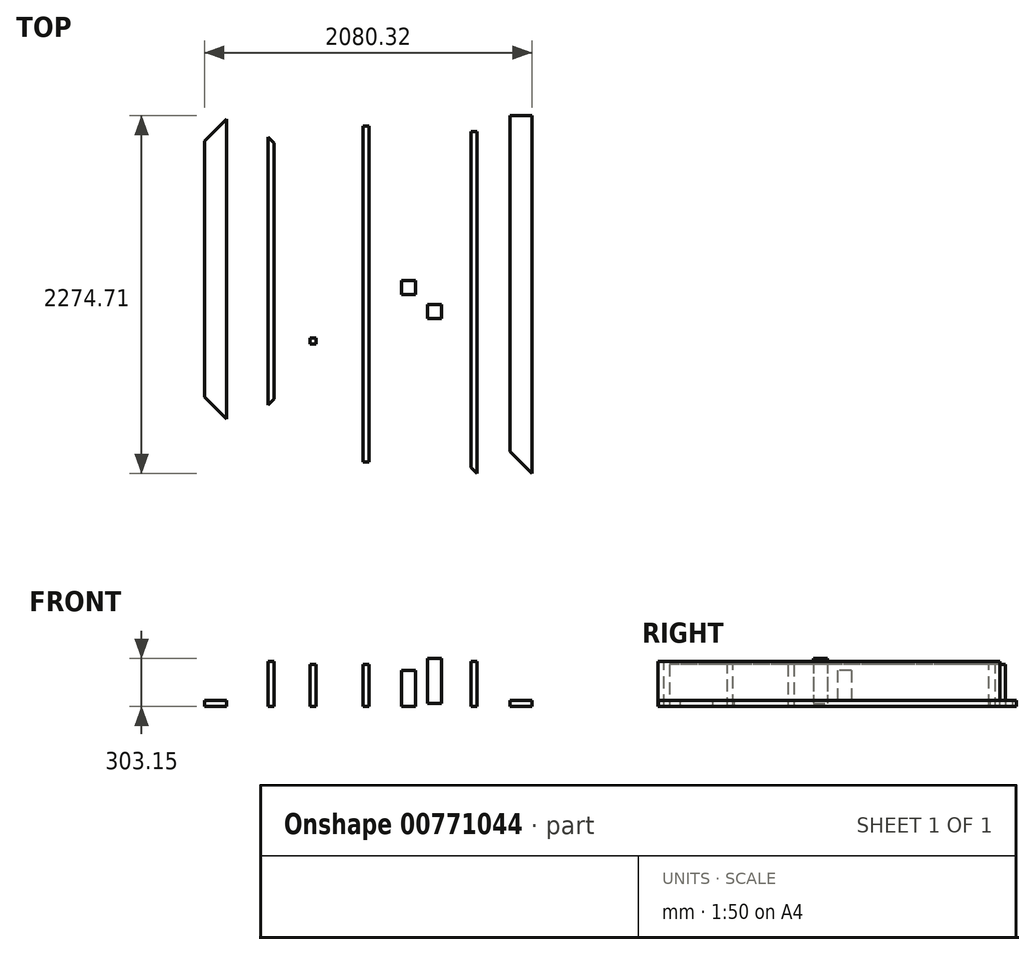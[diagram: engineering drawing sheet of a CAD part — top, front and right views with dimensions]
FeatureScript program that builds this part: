
annotation { "Feature Type Name" : "Feature", "Feature Type Description" : "" }
export const myFeature = defineFeature(function(context is Context, id is Id, definition is map)
    precondition{}
    {
        {
            var Q0;
            Q0=qCreatedBy(makeId("Top.planeOp"),FACE);
            var sketch = newSketch(context, id + "F0", { "sketchPlane" : qUnion([Q0])});
            skLineSegment(sketch, "E0.bottom", {"start": v(19.05, -1075.68) * mm, "end": v(-19.05, -1075.68) * mm});
            skLineSegment(sketch, "E0.top", {"start": v(19.05, 1134.12) * mm, "end": v(-19.05, 1134.12) * mm});
            skLineSegment(sketch, "E0.left", {"start": v(19.05, -1075.68) * mm, "end": v(19.05, 1134.12) * mm});
            skLineSegment(sketch, "E0.right", {"start": v(-19.05, -1075.68) * mm, "end": v(-19.05, 1134.12) * mm});
            skPoint(sketch, "E0.middle", {"position": v(0, 29.22) * mm});
            skSolve(sketch);
        }
        {
            var Q0;
            Q0=makeQuery(id+"F0.imprint","IMPRINT",FACE,{"disambiguationData":[TD([[makeQuery(id+"F0.imprint","IMPRINT",EDGE,{"derivedFrom":sQuery(id+"F0.wireOp",EDGE,"E0.bottom")}),-1.0]])]});
            extrude(context, id + "F1", {"entities" : qUnion([Q0]), "depth" : 285.75 * mm, "offsetDistance" : 25.4 * mm});
        }
        {
            var Q0;
            Q0=makeQuery(id+"F1.opExtrude","CAP_FACE",FACE,{"disambiguationData":[OSD([sQuery(id+"F0.wireOp",EDGE,"E0.bottom"),sQuery(id+"F0.wireOp",EDGE,"E0.top"),sQuery(id+"F0.wireOp",EDGE,"E0.left"),sQuery(id+"F0.wireOp",EDGE,"E0.right")])],"isStart":false});
            var sketch = newSketch(context, id + "F2", { "sketchPlane" : qUnion([Q0])});
            skLineSegment(sketch, "E1", {"start": v(19.05, -1075.68) * mm, "end": v(-19.05, -1075.68) * mm});
            skLineSegment(sketch, "E2", {"start": v(-19.05, -1075.68) * mm, "end": v(-19.05, -1037.58) * mm});
            skLineSegment(sketch, "E3", {"start": v(-19.05, -1037.58) * mm, "end": v(19.05, -1075.68) * mm});
            skSolve(sketch);
        }
        {
            var Q0;
            Q0=makeQuery(id+"F2.imprint","IMPRINT",FACE,{"disambiguationData":[TD([[makeQuery(id+"F2.imprint","IMPRINT",EDGE,{"derivedFrom":sQuery(id+"F2.wireOp",EDGE,"E1")}),-1.0]])]});
            extrude(context, id + "F3", {"entities" : qUnion([Q0]), "operationType" : NewBodyOperationType.REMOVE, "endBound" : BoundingType.THROUGH_ALL, "oppositeDirection" : true, "depth" : 25.4 * mm, "offsetDistance" : 25.4 * mm});
        }
        {
            var Q0;
            Q0=qCreatedBy(makeId("Top.planeOp"),FACE);
            var sketch = newSketch(context, id + "F4", { "sketchPlane" : qUnion([Q0])});
            skLineSegment(sketch, "E4.bottom", {"start": v(-1308.24, 1062.83) * mm, "end": v(-1270.14, 1062.83) * mm});
            skLineSegment(sketch, "E4.top", {"start": v(-1308.24, -638.97) * mm, "end": v(-1270.14, -638.97) * mm});
            skLineSegment(sketch, "E4.left", {"start": v(-1308.24, 1062.83) * mm, "end": v(-1308.24, -638.97) * mm});
            skLineSegment(sketch, "E4.right", {"start": v(-1270.14, 1062.83) * mm, "end": v(-1270.14, -638.97) * mm});
            skSolve(sketch);
        }
        {
            var Q0;
            Q0=makeQuery(id+"F4.imprint","IMPRINT",FACE,{"disambiguationData":[TD([[makeQuery(id+"F4.imprint","IMPRINT",EDGE,{"derivedFrom":sQuery(id+"F4.wireOp",EDGE,"E4.bottom")}),-1.0]])]});
            extrude(context, id + "F5", {"entities" : qUnion([Q0]), "depth" : 285.75 * mm, "offsetDistance" : 25.4 * mm});
        }
        {
            var Q0;
            Q0=makeQuery(id+"F5.opExtrude","CAP_FACE",FACE,{"disambiguationData":[OSD([sQuery(id+"F4.wireOp",EDGE,"E4.bottom"),sQuery(id+"F4.wireOp",EDGE,"E4.top"),sQuery(id+"F4.wireOp",EDGE,"E4.left"),sQuery(id+"F4.wireOp",EDGE,"E4.right")])],"isStart":false});
            var sketch = newSketch(context, id + "F6", { "sketchPlane" : qUnion([Q0])});
            skLineSegment(sketch, "E5", {"start": v(-1270.14, 1062.83) * mm, "end": v(-1308.24, 1062.83) * mm});
            skLineSegment(sketch, "E6", {"start": v(-1308.24, 1062.83) * mm, "end": v(-1270.14, 1024.73) * mm});
            skLineSegment(sketch, "E7", {"start": v(-1270.14, 1024.73) * mm, "end": v(-1270.14, 1062.83) * mm});
            skSolve(sketch);
        }
        {
            var Q0;
            Q0=makeQuery(id+"F6.imprint","IMPRINT",FACE,{"disambiguationData":[TD([[makeQuery(id+"F6.imprint","IMPRINT",EDGE,{"derivedFrom":sQuery(id+"F6.wireOp",EDGE,"E5")}),-1.0]])]});
            extrude(context, id + "F7", {"entities" : qUnion([Q0]), "operationType" : NewBodyOperationType.REMOVE, "endBound" : BoundingType.THROUGH_ALL, "oppositeDirection" : true, "depth" : 25.4 * mm, "offsetDistance" : 25.4 * mm});
        }
        {
            var Q0;
            Q0=makeQuery(id+"F5.opExtrude","CAP_FACE",FACE,{"disambiguationData":[OSD([sQuery(id+"F4.wireOp",EDGE,"E4.bottom"),sQuery(id+"F4.wireOp",EDGE,"E4.top"),sQuery(id+"F4.wireOp",EDGE,"E4.left"),sQuery(id+"F4.wireOp",EDGE,"E4.right")])],"isStart":false});
            var sketch = newSketch(context, id + "F8", { "sketchPlane" : qUnion([Q0])});
            skLineSegment(sketch, "E8", {"start": v(-1308.24, -638.97) * mm, "end": v(-1270.14, -638.97) * mm});
            skLineSegment(sketch, "E9", {"start": v(-1270.14, -638.97) * mm, "end": v(-1270.14, -600.87) * mm});
            skLineSegment(sketch, "E10", {"start": v(-1270.14, -600.87) * mm, "end": v(-1308.24, -638.97) * mm});
            skSolve(sketch);
        }
        {
            var Q0;
            Q0=makeQuery(id+"F8.imprint","IMPRINT",FACE,{"disambiguationData":[TD([[makeQuery(id+"F8.imprint","IMPRINT",EDGE,{"derivedFrom":sQuery(id+"F8.wireOp",EDGE,"E8")}),1.0]])]});
            extrude(context, id + "F9", {"entities" : qUnion([Q0]), "operationType" : NewBodyOperationType.REMOVE, "endBound" : BoundingType.THROUGH_ALL, "oppositeDirection" : true, "depth" : 25.4 * mm, "offsetDistance" : 25.4 * mm});
        }
        {
            var Q0;
            Q0=qCreatedBy(makeId("Top.planeOp"),FACE);
            var sketch = newSketch(context, id + "F10", { "sketchPlane" : qUnion([Q0])});
            skLineSegment(sketch, "E11.bottom", {"start": v(-704.89, 1131.27) * mm, "end": v(-666.79, 1131.27) * mm});
            skLineSegment(sketch, "E11.top", {"start": v(-704.89, -1002.33) * mm, "end": v(-666.79, -1002.33) * mm});
            skLineSegment(sketch, "E11.left", {"start": v(-704.89, 1131.27) * mm, "end": v(-704.89, -1002.33) * mm});
            skLineSegment(sketch, "E11.right", {"start": v(-666.79, 1131.27) * mm, "end": v(-666.79, -1002.33) * mm});
            skSolve(sketch);
        }
        {
            var Q0;
            Q0=makeQuery(id+"F10.imprint","IMPRINT",FACE,{"disambiguationData":[TD([[makeQuery(id+"F10.imprint","IMPRINT",EDGE,{"derivedFrom":sQuery(id+"F10.wireOp",EDGE,"E11.bottom")}),-1.0]])]});
            extrude(context, id + "F11", {"entities" : qUnion([Q0]), "depth" : 266.7 * mm, "offsetDistance" : 25.4 * mm});
        }
        {
            var Q0;
            Q0=qCreatedBy(makeId("Top.planeOp"),FACE);
            var sketch = newSketch(context, id + "F12", { "sketchPlane" : qUnion([Q0])});
            skLineSegment(sketch, "E12.bottom", {"start": v(-1042.75, -212.58) * mm, "end": v(-1004.65, -212.58) * mm});
            skLineSegment(sketch, "E12.top", {"start": v(-1042.75, -250.68) * mm, "end": v(-1004.65, -250.68) * mm});
            skLineSegment(sketch, "E12.left", {"start": v(-1042.75, -212.58) * mm, "end": v(-1042.75, -250.68) * mm});
            skLineSegment(sketch, "E12.right", {"start": v(-1004.65, -212.58) * mm, "end": v(-1004.65, -250.68) * mm});
            skSolve(sketch);
        }
        {
            var Q0;
            Q0=makeQuery(id+"F12.imprint","IMPRINT",FACE,{"disambiguationData":[TD([[makeQuery(id+"F12.imprint","IMPRINT",EDGE,{"derivedFrom":sQuery(id+"F12.wireOp",EDGE,"E12.bottom")}),-1.0]])]});
            extrude(context, id + "F13", {"entities" : qUnion([Q0]), "depth" : 266.7 * mm, "offsetDistance" : 25.4 * mm});
        }
        {
            var Q0;
            Q0=qCreatedBy(makeId("Top.planeOp"),FACE);
            var sketch = newSketch(context, id + "F14", { "sketchPlane" : qUnion([Q0])});
            skLineSegment(sketch, "E13.bottom", {"start": v(-460.84, 151.6) * mm, "end": v(-371.94, 151.6) * mm});
            skLineSegment(sketch, "E13.top", {"start": v(-460.84, 62.7) * mm, "end": v(-371.94, 62.7) * mm});
            skLineSegment(sketch, "E13.left", {"start": v(-460.84, 151.6) * mm, "end": v(-460.84, 62.7) * mm});
            skLineSegment(sketch, "E13.right", {"start": v(-371.94, 151.6) * mm, "end": v(-371.94, 62.7) * mm});
            skSolve(sketch);
        }
        {
            var Q0;
            Q0=makeQuery(id+"F14.imprint","IMPRINT",FACE,{"disambiguationData":[TD([[makeQuery(id+"F14.imprint","IMPRINT",EDGE,{"derivedFrom":sQuery(id+"F14.wireOp",EDGE,"E13.bottom")}),-1.0]])]});
            extrude(context, id + "F15", {"entities" : qUnion([Q0]), "depth" : 228.6 * mm, "offsetDistance" : 25.4 * mm});
        }
        {
            var Q0;
            Q0=qCreatedBy(makeId("Top.planeOp"),FACE);
            var sketch = newSketch(context, id + "F16", { "sketchPlane" : qUnion([Q0])});
            skLineSegment(sketch, "E14.bottom", {"start": v(368.03, 1237.15) * mm, "end": v(228.33, 1237.15) * mm});
            skLineSegment(sketch, "E14.top", {"start": v(368.03, -1074.25) * mm, "end": v(228.33, -1074.25) * mm});
            skLineSegment(sketch, "E14.left", {"start": v(368.03, 1237.15) * mm, "end": v(368.03, -1074.25) * mm});
            skLineSegment(sketch, "E14.right", {"start": v(228.33, 1237.15) * mm, "end": v(228.33, -1074.25) * mm});
            skSolve(sketch);
        }
        {
            var Q0;
            Q0=qSketchRegion(id+"F16",true);
            extrude(context, id + "F17", {"entities" : qUnion([Q0]), "depth" : 38.1 * mm, "offsetDistance" : 25.4 * mm});
        }
        {
            var Q0;
            Q0=makeQuery(id+"F17.opExtrude","CAP_FACE",FACE,{"disambiguationData":[OSD([sQuery(id+"F16.wireOp",EDGE,"E14.bottom"),sQuery(id+"F16.wireOp",EDGE,"E14.top"),sQuery(id+"F16.wireOp",EDGE,"E14.left"),sQuery(id+"F16.wireOp",EDGE,"E14.right")])],"isStart":false});
            var sketch = newSketch(context, id + "F18", { "sketchPlane" : qUnion([Q0])});
            skLineSegment(sketch, "E15", {"start": v(228.33, -1074.25) * mm, "end": v(368.03, -1074.25) * mm});
            skLineSegment(sketch, "E16", {"start": v(368.03, -1074.25) * mm, "end": v(228.33, -934.55) * mm});
            skLineSegment(sketch, "E17", {"start": v(228.33, -934.55) * mm, "end": v(228.33, -1074.25) * mm});
            skSolve(sketch);
        }
        {
            var Q0;
            Q0=makeQuery(id+"F18.imprint","IMPRINT",FACE,{"disambiguationData":[TD([[makeQuery(id+"F18.imprint","IMPRINT",EDGE,{"derivedFrom":sQuery(id+"F18.wireOp",EDGE,"E15")}),-1.0]])]});
            extrude(context, id + "F19", {"entities" : qUnion([Q0]), "operationType" : NewBodyOperationType.REMOVE, "endBound" : BoundingType.THROUGH_ALL, "oppositeDirection" : true, "depth" : 25.4 * mm, "offsetDistance" : 25.4 * mm});
        }
        {
            var Q0;
            Q0=qCreatedBy(makeId("Top.planeOp"),FACE);
            var sketch = newSketch(context, id + "F20", { "sketchPlane" : qUnion([Q0])});
            skLineSegment(sketch, "E18.bottom", {"start": v(-1712.3, 1175.3) * mm, "end": v(-1572.6, 1175.3) * mm});
            skLineSegment(sketch, "E18.top", {"start": v(-1712.3, -729.7) * mm, "end": v(-1572.6, -729.7) * mm});
            skLineSegment(sketch, "E18.left", {"start": v(-1712.3, 1175.3) * mm, "end": v(-1712.3, -729.7) * mm});
            skLineSegment(sketch, "E18.right", {"start": v(-1572.6, 1175.3) * mm, "end": v(-1572.6, -729.7) * mm});
            skSolve(sketch);
        }
        {
            var Q0;
            Q0=makeQuery(id+"F20.imprint","IMPRINT",FACE,{"disambiguationData":[TD([[makeQuery(id+"F20.imprint","IMPRINT",EDGE,{"derivedFrom":sQuery(id+"F20.wireOp",EDGE,"E18.bottom")}),-1.0]])]});
            extrude(context, id + "F21", {"entities" : qUnion([Q0]), "depth" : 38.1 * mm, "offsetDistance" : 25.4 * mm});
        }
        {
            var Q0;
            Q0=makeQuery(id+"F21.opExtrude","CAP_FACE",FACE,{"disambiguationData":[OSD([sQuery(id+"F20.wireOp",EDGE,"E18.bottom"),sQuery(id+"F20.wireOp",EDGE,"E18.top"),sQuery(id+"F20.wireOp",EDGE,"E18.left"),sQuery(id+"F20.wireOp",EDGE,"E18.right")])],"isStart":false});
            var sketch = newSketch(context, id + "F22", { "sketchPlane" : qUnion([Q0])});
            skLineSegment(sketch, "E19", {"start": v(-1572.6, 1175.3) * mm, "end": v(-1712.3, 1175.3) * mm});
            skLineSegment(sketch, "E20", {"start": v(-1712.3, 1175.3) * mm, "end": v(-1712.3, 1035.6) * mm});
            skLineSegment(sketch, "E21", {"start": v(-1712.3, 1035.6) * mm, "end": v(-1572.6, 1175.3) * mm});
            skSolve(sketch);
        }
        {
            var Q0;
            Q0=makeQuery(id+"F22.imprint","IMPRINT",FACE,{"disambiguationData":[TD([[makeQuery(id+"F22.imprint","IMPRINT",EDGE,{"derivedFrom":sQuery(id+"F22.wireOp",EDGE,"E19")}),-1.0]])]});
            extrude(context, id + "F23", {"entities" : qUnion([Q0]), "operationType" : NewBodyOperationType.REMOVE, "endBound" : BoundingType.THROUGH_ALL, "oppositeDirection" : true, "depth" : 25.4 * mm, "offsetDistance" : 25.4 * mm});
        }
        {
            var Q0;
            Q0=makeQuery(id+"F21.opExtrude","CAP_FACE",FACE,{"disambiguationData":[OSD([sQuery(id+"F20.wireOp",EDGE,"E18.bottom"),sQuery(id+"F20.wireOp",EDGE,"E18.top"),sQuery(id+"F20.wireOp",EDGE,"E18.left"),sQuery(id+"F20.wireOp",EDGE,"E18.right")])],"isStart":false});
            var sketch = newSketch(context, id + "F24", { "sketchPlane" : qUnion([Q0])});
            skLineSegment(sketch, "E22", {"start": v(-1572.6, -729.7) * mm, "end": v(-1712.3, -729.7) * mm});
            skLineSegment(sketch, "E23", {"start": v(-1712.3, -729.7) * mm, "end": v(-1712.3, -590) * mm});
            skLineSegment(sketch, "E24", {"start": v(-1712.3, -590) * mm, "end": v(-1572.6, -729.7) * mm});
            skSolve(sketch);
        }
        {
            var Q0;
            Q0=makeQuery(id+"F24.imprint","IMPRINT",FACE,{"disambiguationData":[TD([[makeQuery(id+"F24.imprint","IMPRINT",EDGE,{"derivedFrom":sQuery(id+"F24.wireOp",EDGE,"E22")}),1.0]])]});
            extrude(context, id + "F25", {"entities" : qUnion([Q0]), "operationType" : NewBodyOperationType.REMOVE, "endBound" : BoundingType.THROUGH_ALL, "oppositeDirection" : true, "depth" : 25.4 * mm, "offsetDistance" : 25.4 * mm});
        }
        {
            var Q0;
            Q0=qCreatedBy(makeId("Front.planeOp"),FACE);
            var sketch = newSketch(context, id + "F26", { "sketchPlane" : qUnion([Q0])});
            skLineSegment(sketch, "E25.bottom", {"start": v(-295.59, 303.15) * mm, "end": v(-206.69, 303.15) * mm});
            skLineSegment(sketch, "E25.top", {"start": v(-295.59, 17.4) * mm, "end": v(-206.69, 17.4) * mm});
            skLineSegment(sketch, "E25.left", {"start": v(-295.59, 303.15) * mm, "end": v(-295.59, 17.4) * mm});
            skLineSegment(sketch, "E25.right", {"start": v(-206.69, 303.15) * mm, "end": v(-206.69, 17.4) * mm});
            skSolve(sketch);
        }
        {
            var Q0;
            Q0=makeQuery(id+"F26.imprint","IMPRINT",FACE,{"disambiguationData":[TD([[makeQuery(id+"F26.imprint","IMPRINT",EDGE,{"derivedFrom":sQuery(id+"F26.wireOp",EDGE,"E25.bottom")}),-1.0]])]});
            extrude(context, id + "F27", {"entities" : qUnion([Q0]), "depth" : 88.9 * mm, "offsetDistance" : 25.4 * mm});
        }
        {
            var Q0;
            Q0=makeQuery(id+"F1.opExtrude","CAP_FACE",FACE,{"disambiguationData":[OSD([sQuery(id+"F0.wireOp",EDGE,"E0.bottom"),sQuery(id+"F0.wireOp",EDGE,"E0.top"),sQuery(id+"F0.wireOp",EDGE,"E0.left"),sQuery(id+"F0.wireOp",EDGE,"E0.right")])],"isStart":false});
            var sketch = newSketch(context, id + "F28", { "sketchPlane" : qUnion([Q0])});
            skLineSegment(sketch, "E26", {"start": v(-19.05, 1134.12) * mm, "end": v(19.05, 1134.12) * mm});
            skLineSegment(sketch, "E27", {"start": v(19.05, 1134.12) * mm, "end": v(-19.05, 1096.02) * mm});
            skLineSegment(sketch, "E28", {"start": v(-19.05, 1096.02) * mm, "end": v(-19.05, 1134.12) * mm});
            skSolve(sketch);
        }
        {
            var Q0;
            Q0=makeQuery(id+"F28.imprint","IMPRINT",FACE,{"disambiguationData":[TD([[makeQuery(id+"F28.imprint","IMPRINT",EDGE,{"derivedFrom":sQuery(id+"F28.wireOp",EDGE,"E26")}),1.0]])]});
            extrude(context, id + "F29", {"entities" : qUnion([Q0]), "operationType" : NewBodyOperationType.REMOVE, "endBound" : BoundingType.THROUGH_ALL, "oppositeDirection" : true, "depth" : 25.4 * mm, "offsetDistance" : 25.4 * mm});
        }
        {
            var Q0;
            Q0=makeQuery(id+"F1.opExtrude","CAP_FACE",FACE,{"disambiguationData":[OSD([sQuery(id+"F0.wireOp",EDGE,"E0.bottom"),sQuery(id+"F0.wireOp",EDGE,"E0.top"),sQuery(id+"F0.wireOp",EDGE,"E0.left"),sQuery(id+"F0.wireOp",EDGE,"E0.right")])],"isStart":false});
            var sketch = newSketch(context, id + "F30", { "sketchPlane" : qUnion([Q0])});
            skLineSegment(sketch, "E29", {"start": v(19.05, 1134.12) * mm, "end": v(-19.05, 1096.02) * mm});
            skLineSegment(sketch, "E30", {"start": v(-19.05, 1096.02) * mm, "end": v(19.05, 1096.02) * mm});
            skLineSegment(sketch, "E31", {"start": v(19.05, 1096.02) * mm, "end": v(19.05, 1134.12) * mm});
            skSolve(sketch);
        }
        {
            var Q0;
            Q0=qSketchRegion(id+"F30",true);
            extrude(context, id + "F31", {"entities" : qUnion([Q0]), "operationType" : NewBodyOperationType.REMOVE, "endBound" : BoundingType.THROUGH_ALL, "oppositeDirection" : true, "depth" : 25.4 * mm, "offsetDistance" : 25.4 * mm});
        }
        {
            var Q0;
            Q0=makeQuery(id+"F17.opExtrude","CAP_FACE",FACE,{"disambiguationData":[OSD([sQuery(id+"F16.wireOp",EDGE,"E14.bottom"),sQuery(id+"F16.wireOp",EDGE,"E14.top"),sQuery(id+"F16.wireOp",EDGE,"E14.left"),sQuery(id+"F16.wireOp",EDGE,"E14.right")])],"isStart":false});
            var sketch = newSketch(context, id + "F32", { "sketchPlane" : qUnion([Q0])});
            skLineSegment(sketch, "E32.bottom", {"start": v(228.33, 1237.15) * mm, "end": v(368.03, 1237.15) * mm});
            skLineSegment(sketch, "E32.top", {"start": v(228.33, 1199.03) * mm, "end": v(368.03, 1199.03) * mm});
            skLineSegment(sketch, "E32.left", {"start": v(228.33, 1237.15) * mm, "end": v(228.33, 1199.03) * mm});
            skLineSegment(sketch, "E32.right", {"start": v(368.03, 1237.15) * mm, "end": v(368.03, 1199.03) * mm});
            skSolve(sketch);
        }
        {
            var Q0;
            Q0=qSketchRegion(id+"F32",true);
            extrude(context, id + "F33", {"entities" : qUnion([Q0]), "operationType" : NewBodyOperationType.REMOVE, "endBound" : BoundingType.THROUGH_ALL, "oppositeDirection" : true, "depth" : 25.4 * mm, "offsetDistance" : 25.4 * mm});
        }
    });
